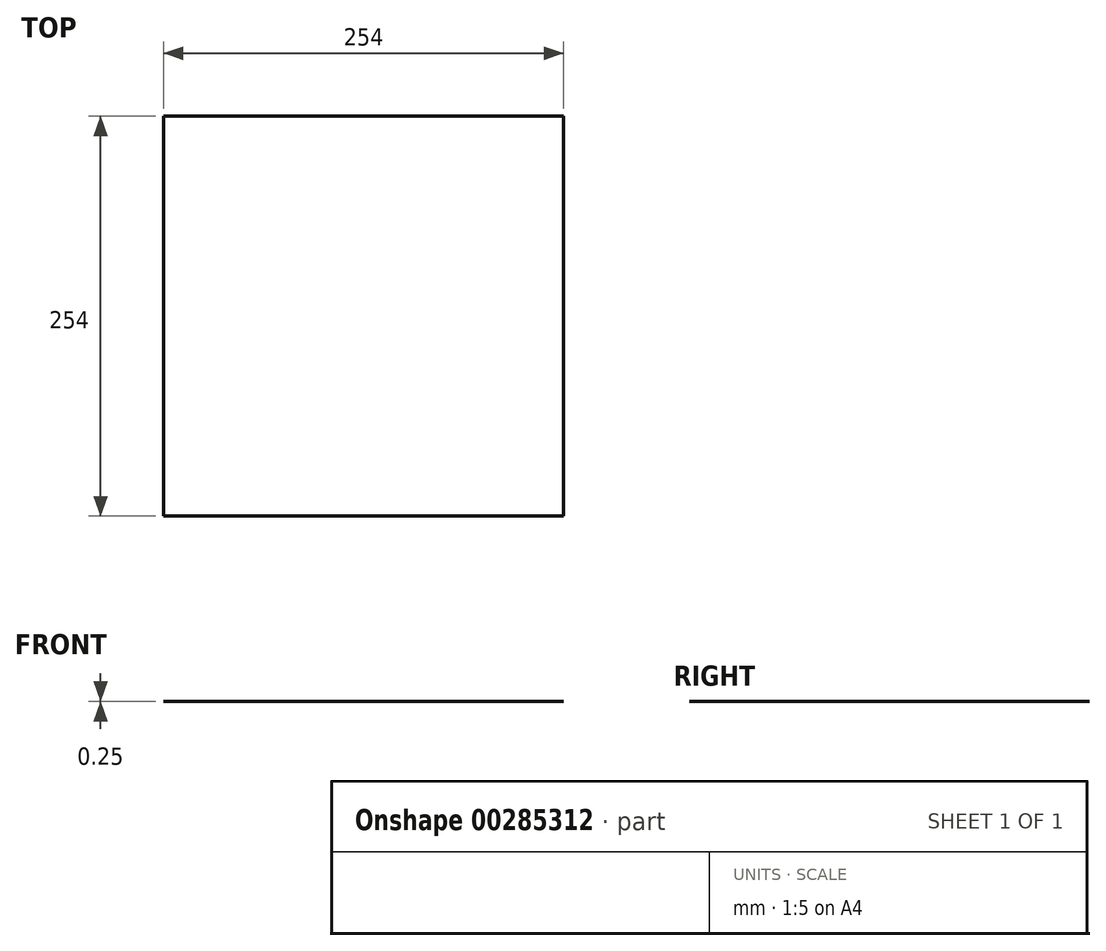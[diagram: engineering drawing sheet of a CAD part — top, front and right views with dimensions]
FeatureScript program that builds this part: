
annotation { "Feature Type Name" : "Feature", "Feature Type Description" : "" }
export const myFeature = defineFeature(function(context is Context, id is Id, definition is map)
    precondition{}
    {
        {
            var Q0;
            Q0=qCreatedBy(makeId("Top.planeOp"),FACE);
            var sketch = newSketch(context, id + "F0", { "sketchPlane" : qUnion([Q0])});
            skLineSegment(sketch, "E0.bottom", {"start": v(-127, 127) * mm, "end": v(127, 127) * mm});
            skLineSegment(sketch, "E0.top", {"start": v(-127, -127) * mm, "end": v(127, -127) * mm});
            skLineSegment(sketch, "E0.left", {"start": v(-127, 127) * mm, "end": v(-127, -127) * mm});
            skLineSegment(sketch, "E0.right", {"start": v(127, 127) * mm, "end": v(127, -127) * mm});
            skPoint(sketch, "E0.middle", {"position": v(0, 0) * mm});
            skSolve(sketch);
        }
        {
            var Q0;
            Q0=makeQuery(id+"F0.imprint","IMPRINT",FACE,{"disambiguationData":[TD([[makeQuery(id+"F0.imprint","IMPRINT",EDGE,{"derivedFrom":sQuery(id+"F0.wireOp",EDGE,"E0.bottom")}),-1.0]])]});
            extrude(context, id + "F1", {"entities" : qUnion([Q0]), "oppositeDirection" : true, "depth" : 0.25 * mm});
        }
    });
